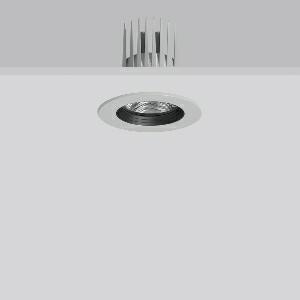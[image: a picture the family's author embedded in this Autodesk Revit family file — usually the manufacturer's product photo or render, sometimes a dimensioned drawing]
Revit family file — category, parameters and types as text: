
# Revit family: heledon_mini_e_901742_004_3_7fd2
name_source: partatom
category: Lighting Fixtures
units: mm (PartAtom-declared; Revit-internal decimal feet)

## family parameters
Cut with Voids When Loaded = No
Host = Face
Light Source = No
Part Type = Normal
Room Calculation Point = No
Round Connector Dimension = Use Diameter
Shared = No

## types (1)
- HELEDON mini E (1 x LED Modul 935, 2650 lm, 3500)
    Apparent Load = 20 VA
    Approval mark = CE
    CIE Flux Codes = 95 99 100 100 100
    Color Rendering = 92
    Color Temperature = 3500
    Default Elevation = 1800 mm
    Description = Series: HELEDON mini
Round recessed downlight. Housing: die-cast aluminium, powder-coated. Black plastic ring and recessed LED to prevent glare from the side. Optical assembly with reflector made of MIRO-Silver with 98% total light reflection for outstanding efficiency - can be changed without tools. Best colour rendering index Ra>90. Suitable for Recessed ceiling mounting. Installation without tools thanks to spring fastening system. Including separate LED converter with connecting cable 600 mm.High quality converter without flickering and stroboscopic effect. Through-wiring box (5 pole) available as accessory. The following accessories can be mounted without use of tools: interchangeable lenses, decorative glasses, honeycomb louvre, clear and frosted diffusers, white interchangeable plastic ring. 
Colour: silver
Diameter: 124 mm
Height: 3 mm
Cut-out diameter: 114 mm
Recess height: 170 mm
Luminaire: recess height: 120 mm
Lamp: LED
Socket: without socket
Colour temperature: 3500K
Colour rendering index (CRI): 92
System power: 20 W
Rated luminous flux: 2650 lm
Luminous efficiency: 133 lm/W
Control gear: Regulated power supply
Protection class: II
Type of protection: IP 20
    Height = 0 mm  [stored 0 ft]
    Lamp = 1 x LED Modul 935
    Lamp Light Flux = 2650 lm
    Lamp count = 1
    Length = 124 mm  [stored 0.406824 ft]
    Lifetime = 50000 h
    Luminous efficacy = 133 lm/W
    Manufacturer = RZB
    ModVariant = No
    Model = 901742.004.3
    Mounting Place = Ceiling
    Mounting Type = Recessed
    Number of Poles = 1
    OnlyDefault = Yes
    Power Factor = 1
    Product Name = HELEDON mini E
    Product group = Recessed downlights
    ProductGroupID = 402
    Protection Class = Protection class II
    Protection Degree = IP 20
    RLX_Detail_Level = 1
    RLX_Emergency_Light_Flux = 0 lm
    RLX_Emergency_Type = 0
    RLX_Emergency_Type_DB = No
    RlxData = <blob elided: 124597 chars, md5=62a5d6a0>
    Socket = socket
    Standby Power = 0 W
    System Light Flux = 2650 lm
    System Power = 20 W
    Type Comments = Product without accessories
    Type Image = 901657.004.jpg
    URL = http://relux.com
    VarID = ---
    Voltage = 230 V
    Voltage Range = 220-240 V
    Weight = 0.00 kg
    Width = 0 mm  [stored 0 ft]

note: [stored X ft] marks values corroborated as IEEE doubles in the binary element streams (Revit-internal decimal feet)

## geometry (parser evidence)
native form markers: Blend x4, Sweep x11
no freeform markers — native parametric forms only
